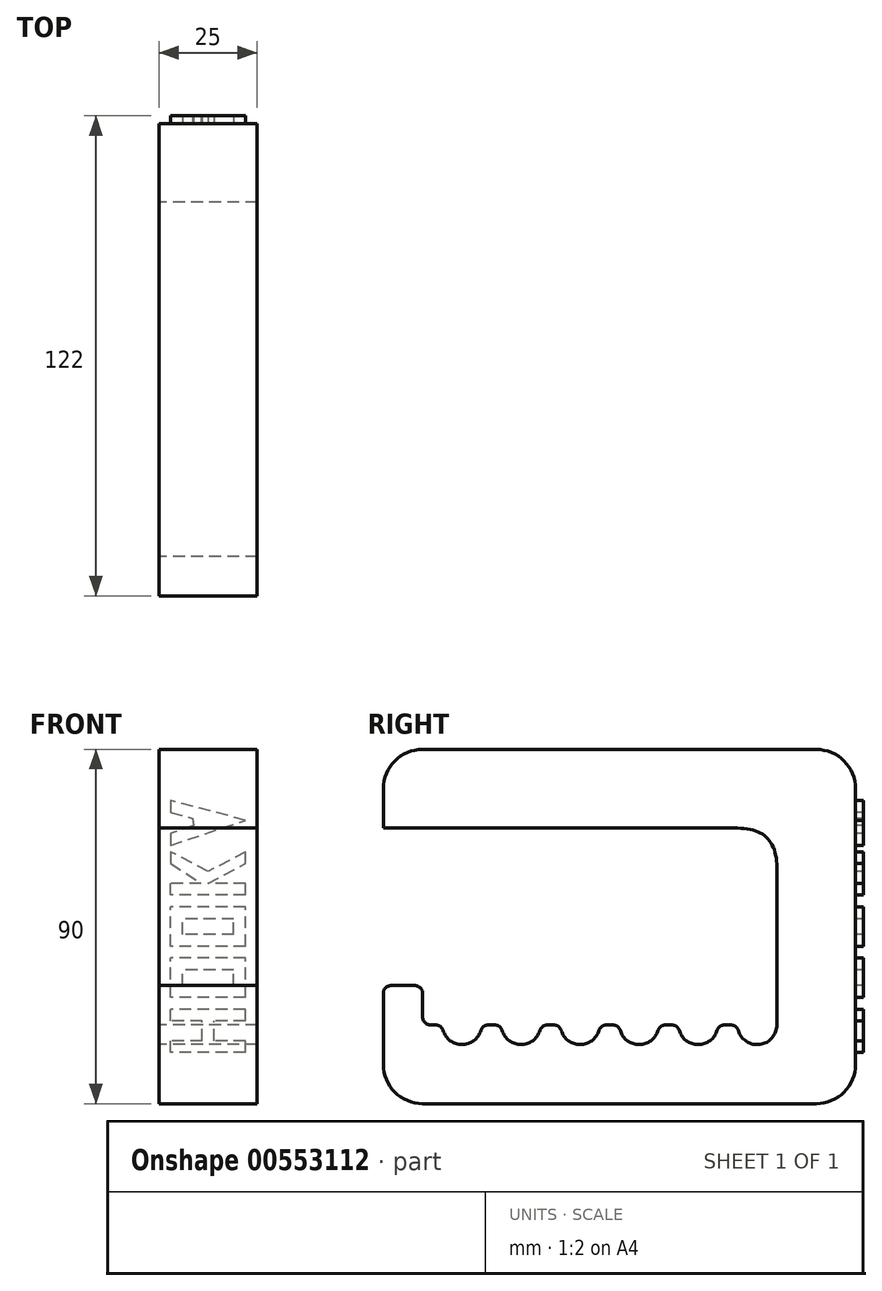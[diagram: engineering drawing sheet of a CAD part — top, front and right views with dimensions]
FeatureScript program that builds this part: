
annotation { "Feature Type Name" : "Feature", "Feature Type Description" : "" }
export const myFeature = defineFeature(function(context is Context, id is Id, definition is map)
    precondition{}
    {
        {
            var Q0;
            Q0=qCreatedBy(makeId("Right.planeOp"),FACE);
            var sketch = newSketch(context, id + "F0", { "sketchPlane" : qUnion([Q0])});
            skLineSegment(sketch, "E0", {"start": v(-120, 0) * mm, "end": v(0, 0) * mm});
            skLineSegment(sketch, "E1", {"start": v(0, 0) * mm, "end": v(0, 90) * mm});
            skLineSegment(sketch, "E2", {"start": v(0, 90) * mm, "end": v(-120, 90) * mm});
            skLineSegment(sketch, "E3", {"start": v(-120, 90) * mm, "end": v(-120, 70) * mm});
            skLineSegment(sketch, "E4", {"start": v(-120, 70) * mm, "end": v(-20, 70) * mm});
            skLineSegment(sketch, "E5", {"start": v(-20, 70) * mm, "end": v(-20, 20) * mm});
            skLineSegment(sketch, "E6", {"start": v(-120, 0) * mm, "end": v(-120, 30) * mm});
            skLineSegment(sketch, "E7", {"start": v(-120, 30) * mm, "end": v(-110, 30) * mm});
            skLineSegment(sketch, "E8", {"start": v(-110, 30) * mm, "end": v(-110, 20) * mm});
            skPoint(sketch, "E9.orphan", {"position": v(-120, 20) * mm});
            skLineSegment(sketch, "E10", {"start": v(-110, 20) * mm, "end": v(-105, 20) * mm});
            skArc(sketch, "E11", {"start": v(-105, 20) * mm, "mid": v(-100, 15) * mm, "end": v(-95, 20) * mm});
            skLineSegment(sketch, "E12", {"start": v(-95, 20) * mm, "end": v(-90, 20) * mm});
            skArc(sketch, "E13", {"start": v(-90, 20) * mm, "mid": v(-85, 15) * mm, "end": v(-80, 20) * mm});
            skLineSegment(sketch, "E14", {"start": v(-80, 20) * mm, "end": v(-75, 20) * mm});
            skArc(sketch, "E15", {"start": v(-75, 20) * mm, "mid": v(-70, 15) * mm, "end": v(-65, 20) * mm});
            skLineSegment(sketch, "E16", {"start": v(-65, 20) * mm, "end": v(-60, 20) * mm});
            skArc(sketch, "E17", {"start": v(-60, 20) * mm, "mid": v(-55, 15) * mm, "end": v(-50, 20) * mm});
            skLineSegment(sketch, "E18", {"start": v(-50, 20) * mm, "end": v(-45, 20) * mm});
            skArc(sketch, "E19", {"start": v(-45, 20) * mm, "mid": v(-40, 15) * mm, "end": v(-35, 20) * mm});
            skLineSegment(sketch, "E20", {"start": v(-35, 20) * mm, "end": v(-30, 20) * mm});
            skArc(sketch, "E21", {"start": v(-30, 20) * mm, "mid": v(-25, 15) * mm, "end": v(-20, 20) * mm});
            skSolve(sketch);
        }
        {
            var Q0;
            Q0=makeQuery(id+"F0.imprint","IMPRINT",FACE,{"disambiguationData":[TD([[makeQuery(id+"F0.imprint","IMPRINT",EDGE,{"derivedFrom":sQuery(id+"F0.wireOp",EDGE,"E0")}),1.0]])]});
            extrude(context, id + "F1", {"entities" : qUnion([Q0]), "depth" : 25 * mm, "offsetDistance" : 25 * mm});
        }
        {
            var Q0;
            Q0=makeQuery(id+"F1.opExtrude","SWEPT_EDGE",EDGE,{"disambiguationData":[OSD([sQuery(id+"F0.wireOp",EDGE,"E2"),sQuery(id+"F0.wireOp",EDGE,"E3")])]});
            var Q1;
            Q1=makeQuery(id+"F1.opExtrude","SWEPT_EDGE",EDGE,{"disambiguationData":[OSD([sQuery(id+"F0.wireOp",EDGE,"E1"),sQuery(id+"F0.wireOp",EDGE,"E2")])]});
            var Q2;
            Q2=makeQuery(id+"F1.opExtrude","SWEPT_EDGE",EDGE,{"disambiguationData":[OSD([sQuery(id+"F0.wireOp",EDGE,"E0"),sQuery(id+"F0.wireOp",EDGE,"E1")])]});
            var Q3;
            Q3=makeQuery(id+"F1.opExtrude","SWEPT_EDGE",EDGE,{"disambiguationData":[OSD([sQuery(id+"F0.wireOp",EDGE,"E0"),sQuery(id+"F0.wireOp",EDGE,"E6")])]});
            fillet(context, id + "F2", {"entities" : qUnion([Q0, Q1, Q2, Q3]), "radius" : 10 * mm, "tangentPropagation" : true, "allowEdgeOverflow" : false});
        }
        {
            var Q0;
            Q0=makeQuery(id+"F1.opExtrude","SWEPT_EDGE",EDGE,{"disambiguationData":[OSD([sQuery(id+"F0.wireOp",EDGE,"E4"),sQuery(id+"F0.wireOp",EDGE,"E5")])]});
            fillet(context, id + "F3", {"entities" : qUnion([Q0]), "radius" : 10 * mm, "tangentPropagation" : true, "rho" : 0.5, "crossSection" : FilletCrossSection.CONIC, "allowEdgeOverflow" : false});
        }
        {
            var Q0;
            Q0=makeQuery(id+"F1.opExtrude","SWEPT_EDGE",EDGE,{"disambiguationData":[OSD([sQuery(id+"F0.wireOp",EDGE,"E6"),sQuery(id+"F0.wireOp",EDGE,"E7")])]});
            var Q1;
            Q1=makeQuery(id+"F1.opExtrude","SWEPT_EDGE",EDGE,{"disambiguationData":[OSD([sQuery(id+"F0.wireOp",EDGE,"E7"),sQuery(id+"F0.wireOp",EDGE,"E8")])]});
            var Q2;
            Q2=makeQuery(id+"F1.opExtrude","SWEPT_EDGE",EDGE,{"disambiguationData":[OSD([sQuery(id+"F0.wireOp",EDGE,"E8"),sQuery(id+"F0.wireOp",EDGE,"E10")])]});
            var Q3;
            Q3=makeQuery(id+"F1.opExtrude","SWEPT_EDGE",EDGE,{"disambiguationData":[OSD([sQuery(id+"F0.wireOp",EDGE,"E10"),sQuery(id+"F0.wireOp",EDGE,"E11")])]});
            var Q4;
            Q4=makeQuery(id+"F1.opExtrude","SWEPT_EDGE",EDGE,{"disambiguationData":[OSD([sQuery(id+"F0.wireOp",EDGE,"E11"),sQuery(id+"F0.wireOp",EDGE,"E12")])]});
            var Q5;
            Q5=makeQuery(id+"F1.opExtrude","SWEPT_EDGE",EDGE,{"disambiguationData":[OSD([sQuery(id+"F0.wireOp",EDGE,"E12"),sQuery(id+"F0.wireOp",EDGE,"E13")])]});
            var Q6;
            Q6=makeQuery(id+"F1.opExtrude","SWEPT_EDGE",EDGE,{"disambiguationData":[OSD([sQuery(id+"F0.wireOp",EDGE,"E13"),sQuery(id+"F0.wireOp",EDGE,"E14")])]});
            var Q7;
            Q7=makeQuery(id+"F1.opExtrude","SWEPT_EDGE",EDGE,{"disambiguationData":[OSD([sQuery(id+"F0.wireOp",EDGE,"E14"),sQuery(id+"F0.wireOp",EDGE,"E15")])]});
            var Q8;
            Q8=makeQuery(id+"F1.opExtrude","SWEPT_EDGE",EDGE,{"disambiguationData":[OSD([sQuery(id+"F0.wireOp",EDGE,"E15"),sQuery(id+"F0.wireOp",EDGE,"E16")])]});
            var Q9;
            Q9=makeQuery(id+"F1.opExtrude","SWEPT_EDGE",EDGE,{"disambiguationData":[OSD([sQuery(id+"F0.wireOp",EDGE,"E16"),sQuery(id+"F0.wireOp",EDGE,"E17")])]});
            var Q10;
            Q10=makeQuery(id+"F1.opExtrude","SWEPT_EDGE",EDGE,{"disambiguationData":[OSD([sQuery(id+"F0.wireOp",EDGE,"E17"),sQuery(id+"F0.wireOp",EDGE,"E18")])]});
            var Q11;
            Q11=makeQuery(id+"F1.opExtrude","SWEPT_EDGE",EDGE,{"disambiguationData":[OSD([sQuery(id+"F0.wireOp",EDGE,"E18"),sQuery(id+"F0.wireOp",EDGE,"E19")])]});
            var Q12;
            Q12=makeQuery(id+"F1.opExtrude","SWEPT_EDGE",EDGE,{"disambiguationData":[OSD([sQuery(id+"F0.wireOp",EDGE,"E19"),sQuery(id+"F0.wireOp",EDGE,"E20")])]});
            var Q13;
            Q13=makeQuery(id+"F1.opExtrude","SWEPT_EDGE",EDGE,{"disambiguationData":[OSD([sQuery(id+"F0.wireOp",EDGE,"E20"),sQuery(id+"F0.wireOp",EDGE,"E21")])]});
            fillet(context, id + "F4", {"entities" : qUnion([Q0, Q1, Q2, Q3, Q4, Q5, Q6, Q7, Q8, Q9, Q10, Q11, Q12, Q13]), "radius" : 2 * mm, "tangentPropagation" : true, "allowEdgeOverflow" : false});
        }
        {
            var Q0;
            Q0=makeQuery(id+"F1.opExtrude","SWEPT_FACE",FACE,{"disambiguationData":[OSD([sQuery(id+"F0.wireOp",EDGE,"E1")])]});
            var sketch = newSketch(context, id + "F5", { "sketchPlane" : qUnion([Q0])});
            skLineSegment(sketch, "E22.bottom", {"start": v(-22, 13) * mm, "end": v(-3, 13) * mm, "construction": true});
            skLineSegment(sketch, "E22.top", {"start": v(-22, 77) * mm, "end": v(-3, 77) * mm, "construction": true});
            skLineSegment(sketch, "E22.left", {"start": v(-22, 13) * mm, "end": v(-22, 77) * mm, "construction": true});
            skLineSegment(sketch, "E22.right", {"start": v(-3, 13) * mm, "end": v(-3, 77) * mm, "construction": true});
            skLineSegment(sketch, "E23.bottom", {"start": v(-22, 13) * mm, "end": v(-3, 13) * mm});
            skLineSegment(sketch, "E23.top", {"start": v(-22, 16) * mm, "end": v(-14, 16) * mm});
            skLineSegment(sketch, "E23.left", {"start": v(-22, 13) * mm, "end": v(-22, 16) * mm});
            skLineSegment(sketch, "E23.right", {"start": v(-3, 13) * mm, "end": v(-3, 16) * mm});
            skLineSegment(sketch, "E24.left", {"start": v(-14, 16) * mm, "end": v(-14, 21) * mm});
            skLineSegment(sketch, "E24.right", {"start": v(-11, 16) * mm, "end": v(-11, 21) * mm});
            skLineSegment(sketch, "E25.bottom", {"start": v(-22, 21) * mm, "end": v(-14, 21) * mm});
            skLineSegment(sketch, "E25.top", {"start": v(-22, 24) * mm, "end": v(-3, 24) * mm});
            skLineSegment(sketch, "E25.left", {"start": v(-22, 21) * mm, "end": v(-22, 24) * mm});
            skLineSegment(sketch, "E25.right", {"start": v(-3, 21) * mm, "end": v(-3, 24) * mm});
            skLineSegment(sketch, "E26.trimOffspring", {"start": v(-11, 21) * mm, "end": v(-3, 21) * mm});
            skLineSegment(sketch, "E27.trimOffspring", {"start": v(-11, 16) * mm, "end": v(-3, 16) * mm});
            skLineSegment(sketch, "E28.bottom", {"start": v(-22, 27) * mm, "end": v(-3, 27) * mm});
            skLineSegment(sketch, "E28.top", {"start": v(-22, 37) * mm, "end": v(-3, 37) * mm});
            skLineSegment(sketch, "E28.left", {"start": v(-22, 27) * mm, "end": v(-22, 37) * mm});
            skLineSegment(sketch, "E28.right", {"start": v(-3, 27) * mm, "end": v(-3, 37) * mm});
            skLineSegment(sketch, "E29.bottom", {"start": v(-22, 40) * mm, "end": v(-3, 40) * mm});
            skLineSegment(sketch, "E29.top", {"start": v(-22, 50) * mm, "end": v(-3, 50) * mm});
            skLineSegment(sketch, "E29.left", {"start": v(-22, 40) * mm, "end": v(-22, 50) * mm});
            skLineSegment(sketch, "E29.right", {"start": v(-3, 40) * mm, "end": v(-3, 50) * mm});
            skLineSegment(sketch, "E30.bottom", {"start": v(-19, 30) * mm, "end": v(-6, 30) * mm});
            skLineSegment(sketch, "E30.top", {"start": v(-19, 34) * mm, "end": v(-6, 34) * mm});
            skLineSegment(sketch, "E30.left", {"start": v(-19, 30) * mm, "end": v(-19, 34) * mm});
            skLineSegment(sketch, "E30.right", {"start": v(-6, 30) * mm, "end": v(-6, 34) * mm});
            skLineSegment(sketch, "E31.bottom", {"start": v(-19, 43) * mm, "end": v(-6, 43) * mm});
            skLineSegment(sketch, "E31.top", {"start": v(-19, 47) * mm, "end": v(-6, 47) * mm});
            skLineSegment(sketch, "E31.left", {"start": v(-19, 43) * mm, "end": v(-19, 47) * mm});
            skLineSegment(sketch, "E31.right", {"start": v(-6, 43) * mm, "end": v(-6, 47) * mm});
            skLineSegment(sketch, "E32.bottom", {"start": v(-22, 53) * mm, "end": v(-3, 53) * mm});
            skLineSegment(sketch, "E32.top", {"start": v(-22, 56) * mm, "end": v(-12.5, 56) * mm});
            skLineSegment(sketch, "E32.left", {"start": v(-22, 53) * mm, "end": v(-22, 56) * mm});
            skLineSegment(sketch, "E32.right", {"start": v(-3, 53) * mm, "end": v(-3, 56) * mm});
            skLineSegment(sketch, "E33", {"start": v(-12.5, 56) * mm, "end": v(-22, 61) * mm});
            skLineSegment(sketch, "E34", {"start": v(-22, 61) * mm, "end": v(-22, 64) * mm});
            skLineSegment(sketch, "E35", {"start": v(-22, 64) * mm, "end": v(-12.5, 59) * mm});
            skLineSegment(sketch, "E36", {"start": v(-12.5, 59) * mm, "end": v(-3, 64) * mm});
            skLineSegment(sketch, "E37", {"start": v(-3, 64) * mm, "end": v(-3, 61) * mm});
            skLineSegment(sketch, "E38", {"start": v(-3, 65.61) * mm, "end": v(-22, 72) * mm});
            skLineSegment(sketch, "E39", {"start": v(-22, 72) * mm, "end": v(-3, 77) * mm});
            skLineSegment(sketch, "E40", {"start": v(-8.81, 70.73) * mm, "end": v(-3, 68.61) * mm});
            skLineSegment(sketch, "E41", {"start": v(-3, 68.61) * mm, "end": v(-3, 65.61) * mm});
            skLineSegment(sketch, "E42", {"start": v(-3, 77) * mm, "end": v(-3, 74) * mm});
            skLineSegment(sketch, "E43", {"start": v(-3, 74) * mm, "end": v(-8.57, 72.5) * mm});
            skLineSegment(sketch, "E44", {"start": v(-8.57, 72.5) * mm, "end": v(-8.81, 70.73) * mm});
            skLineSegment(sketch, "E45", {"start": v(-3, 61) * mm, "end": v(-10.73, 56) * mm});
            skLineSegment(sketch, "E46.trimOffspring", {"start": v(-10.73, 56) * mm, "end": v(-3, 56) * mm});
            skSolve(sketch);
        }
        {
            var Q0;
            Q0 = qSketchRegion(id + "F5", true);
            extrude(context, id + "F6", {"entities" : qUnion([Q0]), "operationType" : NewBodyOperationType.ADD, "depth" : 2 * mm, "offsetDistance" : 25 * mm});
        }
    });
